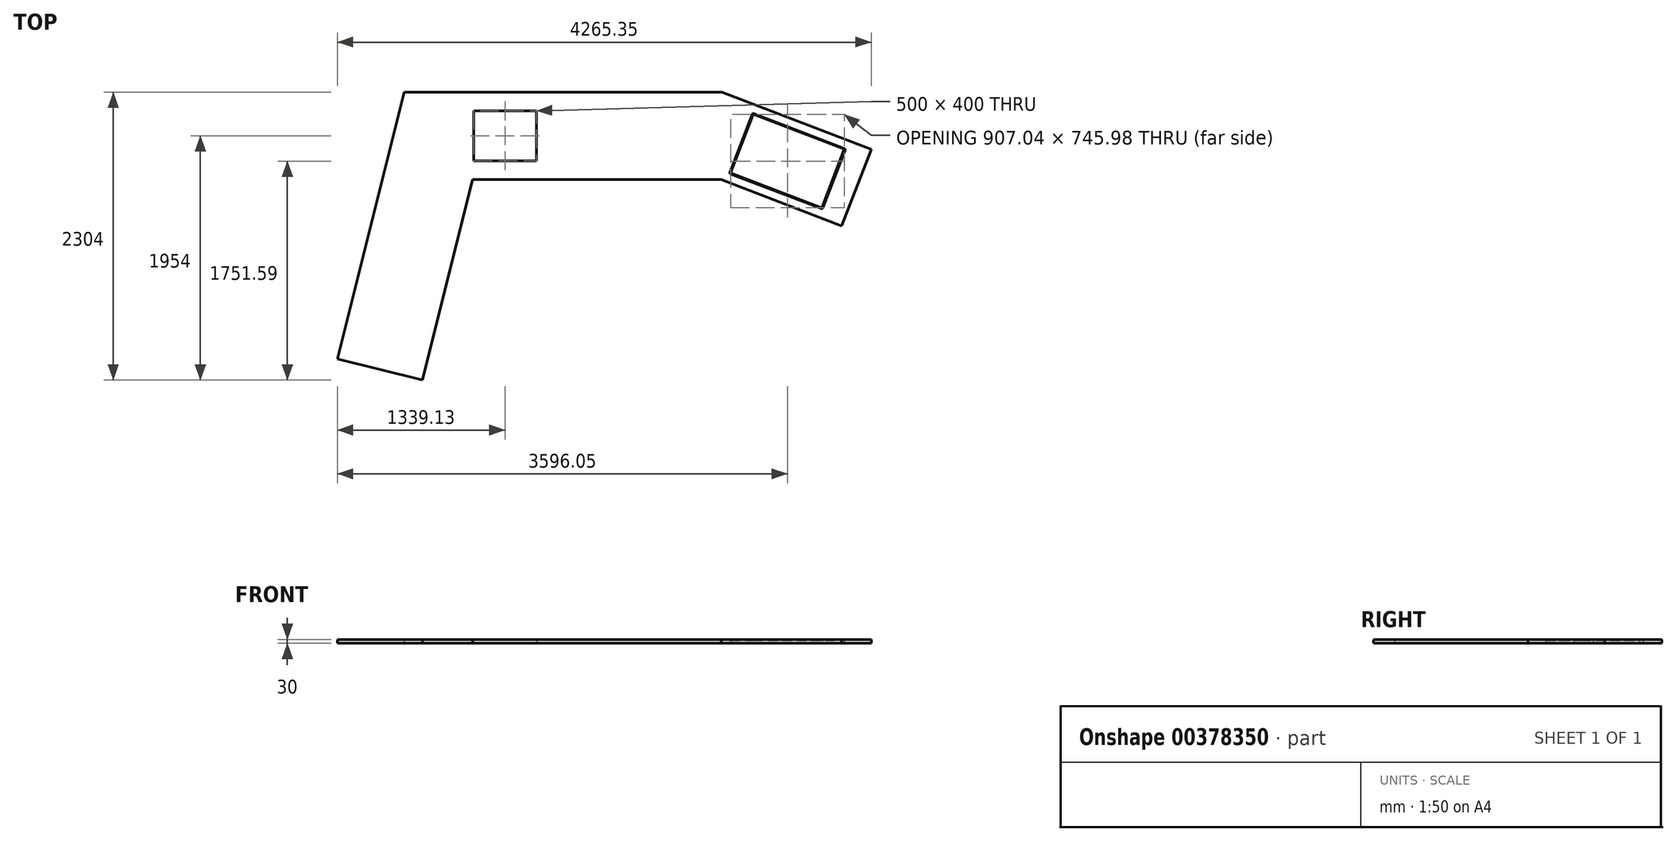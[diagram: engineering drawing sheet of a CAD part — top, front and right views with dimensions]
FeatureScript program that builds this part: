
annotation { "Feature Type Name" : "Feature", "Feature Type Description" : "" }
export const myFeature = defineFeature(function(context is Context, id is Id, definition is map)
    precondition{}
    {
        {
            var Q0;
            Q0=qCreatedBy(makeId("Top.planeOp"),FACE);
            var sketch = newSketch(context, id + "F0", { "sketchPlane" : qUnion([Q0])});
            skLineSegment(sketch, "E0.bottom", {"start": v(655.23, -350) * mm, "end": v(-1330.9, -350) * mm});
            skLineSegment(sketch, "E0.top", {"start": v(662.2, 350) * mm, "end": v(-1877.8, 350) * mm});
            skPoint(sketch, "E0.middle", {"position": v(0, 0) * mm});
            skLineSegment(sketch, "E1", {"start": v(-1877.8, 350) * mm, "end": v(-2410.04, -1784.65) * mm});
            skLineSegment(sketch, "E2", {"start": v(-2410.04, -1784.65) * mm, "end": v(-1730.83, -1954) * mm});
            skLineSegment(sketch, "E3", {"start": v(-1730.83, -1954) * mm, "end": v(-1330.9, -350) * mm});
            skLineSegment(sketch, "E4", {"start": v(662.2, 350) * mm, "end": v(1855.3, -108) * mm});
            skLineSegment(sketch, "E5", {"start": v(1855.3, -108) * mm, "end": v(1620.22, -720.42) * mm});
            skLineSegment(sketch, "E6", {"start": v(1620.22, -720.42) * mm, "end": v(655.23, -350) * mm});
            skPoint(sketch, "E7.orphan", {"position": v(1877.8, -350) * mm});
            skLineSegment(sketch, "E8.bottom", {"start": v(-1320.9, 200) * mm, "end": v(-820.9, 200) * mm});
            skLineSegment(sketch, "E8.top", {"start": v(-1320.9, -200) * mm, "end": v(-820.9, -200) * mm});
            skLineSegment(sketch, "E8.left", {"start": v(-1320.9, 200) * mm, "end": v(-1320.9, -200) * mm});
            skLineSegment(sketch, "E8.right", {"start": v(-820.9, 200) * mm, "end": v(-820.9, -200) * mm});
            skLineSegment(sketch, "E9", {"start": v(915.6, 170.25) * mm, "end": v(1636.33, -106.41) * mm});
            skLineSegment(sketch, "E10", {"start": v(1639.2, -112.87) * mm, "end": v(1462.89, -572.2) * mm});
            skLineSegment(sketch, "E11", {"start": v(1456.43, -575.07) * mm, "end": v(735.7, -298.41) * mm});
            skLineSegment(sketch, "E12", {"start": v(732.83, -291.95) * mm, "end": v(909.14, 167.37) * mm});
            skPoint(sketch, "E13.visualSharp", {"position": v(910.94, 172.04) * mm});
            skArc(sketch, "E13.filletArc", {"start": v(915.6, 170.25) * mm, "mid": v(911.78, 170.15) * mm, "end": v(909.14, 167.37) * mm});
            skPoint(sketch, "E14.visualSharp", {"position": v(731.04, -296.62) * mm});
            skArc(sketch, "E14.filletArc", {"start": v(732.83, -291.95) * mm, "mid": v(732.93, -295.78) * mm, "end": v(735.7, -298.41) * mm});
            skPoint(sketch, "E15.visualSharp", {"position": v(1461.1, -576.86) * mm});
            skArc(sketch, "E15.filletArc", {"start": v(1456.43, -575.07) * mm, "mid": v(1460.25, -574.97) * mm, "end": v(1462.89, -572.2) * mm});
            skPoint(sketch, "E16.visualSharp", {"position": v(1641, -108.2) * mm});
            skArc(sketch, "E16.filletArc", {"start": v(1639.2, -112.87) * mm, "mid": v(1639.1, -109.05) * mm, "end": v(1636.33, -106.41) * mm});
            skSolve(sketch);
        }
        {
            var Q0;
            Q0 = qSketchRegion(id + "F0", true);
            extrude(context, id + "F1", {"entities" : qUnion([Q0]), "depth" : 30 * mm});
        }
        {
            var Q0;
            Q0=makeQuery(id+"F1.opExtrude","CAP_FACE",FACE,{"disambiguationData":[OSD([sQuery(id+"F0.wireOp",EDGE,"E0.bottom"),sQuery(id+"F0.wireOp",EDGE,"E0.top"),sQuery(id+"F0.wireOp",EDGE,"E1"),sQuery(id+"F0.wireOp",EDGE,"E2"),sQuery(id+"F0.wireOp",EDGE,"E3"),sQuery(id+"F0.wireOp",EDGE,"E4"),sQuery(id+"F0.wireOp",EDGE,"E5"),sQuery(id+"F0.wireOp",EDGE,"E6"),sQuery(id+"F0.wireOp",EDGE,"E8.bottom"),sQuery(id+"F0.wireOp",EDGE,"E8.top"),sQuery(id+"F0.wireOp",EDGE,"E8.left"),sQuery(id+"F0.wireOp",EDGE,"E8.right"),sQuery(id+"F0.wireOp",EDGE,"E9"),sQuery(id+"F0.wireOp",EDGE,"E10"),sQuery(id+"F0.wireOp",EDGE,"E11"),sQuery(id+"F0.wireOp",EDGE,"E12"),sQuery(id+"F0.wireOp",EDGE,"E13.filletArc"),sQuery(id+"F0.wireOp",EDGE,"E14.filletArc"),sQuery(id+"F0.wireOp",EDGE,"E15.filletArc"),sQuery(id+"F0.wireOp",EDGE,"E16.filletArc")])],"isStart":false});
            var sketch = newSketch(context, id + "F2", { "sketchPlane" : qUnion([Q0])});
            skLineSegment(sketch, "E17", {"start": v(916.25, 177.5) * mm, "end": v(1640.7, -100.6) * mm});
            skLineSegment(sketch, "E18", {"start": v(1646.46, -113.52) * mm, "end": v(1468.7, -576.57) * mm});
            skLineSegment(sketch, "E19", {"start": v(1455.79, -582.32) * mm, "end": v(731.33, -304.23) * mm});
            skLineSegment(sketch, "E20", {"start": v(903.33, 171.75) * mm, "end": v(725.58, -291.31) * mm});
            skPoint(sketch, "E21.visualSharp", {"position": v(906.9, 181.08) * mm});
            skArc(sketch, "E21.filletArc", {"start": v(916.25, 177.5) * mm, "mid": v(908.6, 177.3) * mm, "end": v(903.33, 171.75) * mm});
            skPoint(sketch, "E22.visualSharp", {"position": v(722, -300.65) * mm});
            skArc(sketch, "E22.filletArc", {"start": v(725.58, -291.31) * mm, "mid": v(725.78, -298.96) * mm, "end": v(731.33, -304.23) * mm});
            skPoint(sketch, "E23.visualSharp", {"position": v(1465.12, -585.9) * mm});
            skArc(sketch, "E23.filletArc", {"start": v(1455.79, -582.32) * mm, "mid": v(1463.44, -582.12) * mm, "end": v(1468.7, -576.57) * mm});
            skPoint(sketch, "E24.visualSharp", {"position": v(1650.04, -104.18) * mm});
            skArc(sketch, "E24.filletArc", {"start": v(1646.46, -113.52) * mm, "mid": v(1646.26, -105.86) * mm, "end": v(1640.7, -100.6) * mm});
            skSolve(sketch);
        }
        {
            var Q0;
            Q0 = qSketchRegion(id + "F2", true);
            extrude(context, id + "F3", {"entities" : qUnion([Q0]), "operationType" : NewBodyOperationType.REMOVE, "oppositeDirection" : true, "depth" : 6.5 * mm});
        }
    });
